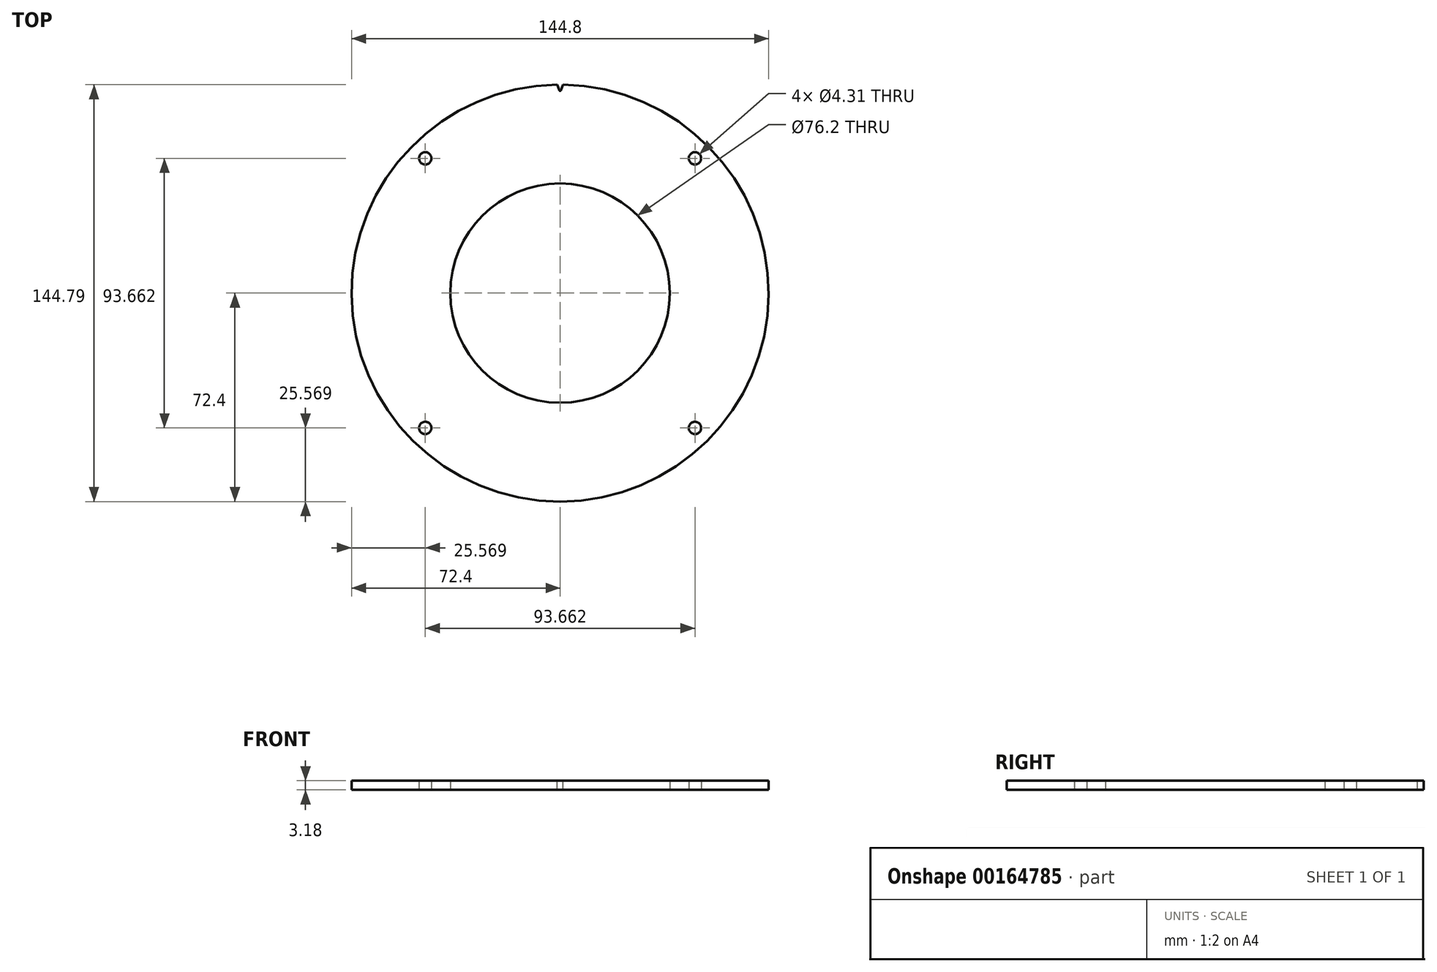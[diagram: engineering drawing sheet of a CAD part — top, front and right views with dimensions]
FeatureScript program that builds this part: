
annotation { "Feature Type Name" : "Feature", "Feature Type Description" : "" }
export const myFeature = defineFeature(function(context is Context, id is Id, definition is map)
    precondition{}
    {
        {
            var Q0;
            Q0=qCreatedBy(makeId("Top.planeOp"),FACE);
            var sketch = newSketch(context, id + "F0", { "sketchPlane" : qUnion([Q0])});
            skCircle(sketch, "E0", {"center": v(0, 0) * mm, "radius": 72.4 * mm});
            skCircle(sketch, "E1", {"center": v(0, 0) * mm, "radius": 70.2 * mm, "construction": true});
            skLineSegment(sketch, "E2.bottom", {"start": v(-46.83, 46.83) * mm, "end": v(46.83, 46.83) * mm, "construction": true});
            skLineSegment(sketch, "E2.top", {"start": v(-46.83, -46.83) * mm, "end": v(46.83, -46.83) * mm, "construction": true});
            skLineSegment(sketch, "E2.left", {"start": v(-46.83, 46.83) * mm, "end": v(-46.83, -46.83) * mm, "construction": true});
            skLineSegment(sketch, "E2.right", {"start": v(46.83, 46.83) * mm, "end": v(46.83, -46.83) * mm, "construction": true});
            skCircle(sketch, "E3", {"center": v(-46.83, 46.83) * mm, "radius": 3.97 * mm, "construction": true});
            skCircle(sketch, "E4", {"center": v(-46.83, 46.83) * mm, "radius": 2.15 * mm});
            skCircle(sketch, "E5", {"center": v(46.83, 46.83) * mm, "radius": 2.15 * mm});
            skCircle(sketch, "E6", {"center": v(46.83, -46.83) * mm, "radius": 2.15 * mm});
            skCircle(sketch, "E7", {"center": v(-46.83, -46.83) * mm, "radius": 2.15 * mm});
            skCircle(sketch, "E8", {"center": v(0, 0) * mm, "radius": 38.1 * mm});
            skSolve(sketch);
        }
        {
            var Q0;
            Q0 = qSketchRegion(id + "F0", true);
            extrude(context, id + "F1", {"entities" : qUnion([Q0]), "depth" : 3.17 * mm});
        }
        {
            var Q0;
            Q0=makeQuery(id+"F1.opExtrude","CAP_FACE",FACE,{"disambiguationData":[OSD([sQuery(id+"F0.wireOp",EDGE,"E0"),sQuery(id+"F0.wireOp",EDGE,"E4"),sQuery(id+"F0.wireOp",EDGE,"E5"),sQuery(id+"F0.wireOp",EDGE,"E6"),sQuery(id+"F0.wireOp",EDGE,"E7")])],"isStart":false});
            var sketch = newSketch(context, id + "F2", { "sketchPlane" : qUnion([Q0])});
            skLineSegment(sketch, "E9", {"start": v(0, 0) * mm, "end": v(0, 72.4) * mm, "construction": true});
            skArc(sketch, "E10", {"start": v(1.02, 72.4) * mm, "mid": v(0, 72.4) * mm, "end": v(-1.02, 72.4) * mm});
            skLineSegment(sketch, "E11", {"start": v(-1.02, 72.4) * mm, "end": v(-0.28, 70.42) * mm});
            skLineSegment(sketch, "E12", {"start": v(1.02, 72.4) * mm, "end": v(0.28, 70.42) * mm});
            skArc(sketch, "E13", {"start": v(-0.28, 70.42) * mm, "mid": v(0, 70.23) * mm, "end": v(0.28, 70.42) * mm});
            skLineSegment(sketch, "E14", {"start": v(0, 0) * mm, "end": v(0.66, 72.4) * mm, "construction": true});
            skPoint(sketch, "E15", {"position": v(0.65, 71.4) * mm});
            skSolve(sketch);
        }
        {
            var Q0;
            Q0 = qSketchRegion(id + "F2", true);
            var Q1;
            Q1=makeQuery(id+"F1.opExtrude","CAP_FACE",FACE,{"disambiguationData":[OSD([sQuery(id+"F0.wireOp",EDGE,"E0"),sQuery(id+"F0.wireOp",EDGE,"E4"),sQuery(id+"F0.wireOp",EDGE,"E5"),sQuery(id+"F0.wireOp",EDGE,"E6"),sQuery(id+"F0.wireOp",EDGE,"E7")])],"isStart":true});
            extrude(context, id + "F3", {"entities" : qUnion([Q0]), "operationType" : NewBodyOperationType.REMOVE, "endBound" : BoundingType.UP_TO_SURFACE, "oppositeDirection" : true, "endBoundEntityFace" : qUnion([Q1]), "depth" : 25.4 * mm});
        }
    });
